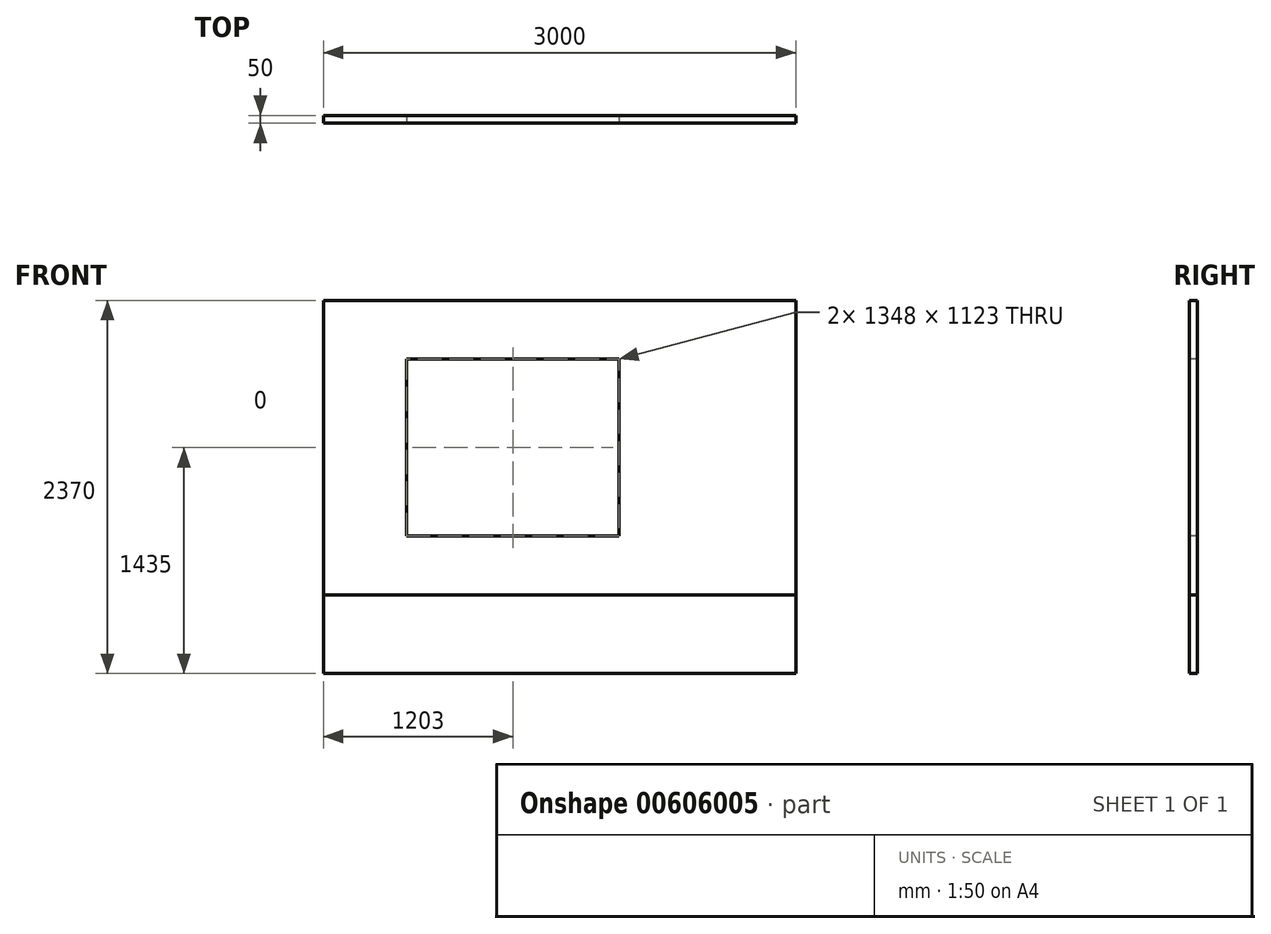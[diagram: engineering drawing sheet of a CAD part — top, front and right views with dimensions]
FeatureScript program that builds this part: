
annotation { "Feature Type Name" : "Feature", "Feature Type Description" : "" }
export const myFeature = defineFeature(function(context is Context, id is Id, definition is map)
    precondition{}
    {
        {
            var Q0;
            Q0=qCreatedBy(makeId("Front.planeOp"),FACE);
            var sketch = newSketch(context, id + "F0", { "sketchPlane" : qUnion([Q0])});
            skLineSegment(sketch, "E0.bottom", {"start": v(1500, -935) * mm, "end": v(-1500, -935) * mm});
            skLineSegment(sketch, "E0.top", {"start": v(1500, 935) * mm, "end": v(-1500, 935) * mm});
            skLineSegment(sketch, "E0.left", {"start": v(1500, -935) * mm, "end": v(1500, 935) * mm});
            skLineSegment(sketch, "E0.right", {"start": v(-1500, -935) * mm, "end": v(-1500, 935) * mm});
            skPoint(sketch, "E0.middle", {"position": v(0, 0) * mm});
            skSolve(sketch);
        }
        {
            var Q0;
            Q0=makeQuery(id+"F0.imprint","IMPRINT",FACE,{"disambiguationData":[TD([[makeQuery(id+"F0.imprint","IMPRINT",EDGE,{"derivedFrom":sQuery(id+"F0.wireOp",EDGE,"E0.bottom")}),-1.0]])]});
            extrude(context, id + "F1", {"entities" : qUnion([Q0]), "depth" : 50 * mm, "offsetDistance" : 25 * mm});
        }
        {
            var Q0;
            Q0=makeQuery(id+"F1.opExtrude","CAP_FACE",FACE,{"disambiguationData":[OSD([sQuery(id+"F0.wireOp",EDGE,"E0.bottom"),sQuery(id+"F0.wireOp",EDGE,"E0.top"),sQuery(id+"F0.wireOp",EDGE,"E0.left"),sQuery(id+"F0.wireOp",EDGE,"E0.right")])],"isStart":false});
            var sketch = newSketch(context, id + "F2", { "sketchPlane" : qUnion([Q0])});
            skLineSegment(sketch, "E1.bottom", {"start": v(-971, 561.5) * mm, "end": v(377, 561.5) * mm});
            skLineSegment(sketch, "E1.top", {"start": v(-971, -561.5) * mm, "end": v(377, -561.5) * mm});
            skLineSegment(sketch, "E1.left", {"start": v(-971, 561.5) * mm, "end": v(-971, -561.5) * mm});
            skLineSegment(sketch, "E1.right", {"start": v(377, 561.5) * mm, "end": v(377, -561.5) * mm});
            skSolve(sketch);
        }
        {
            var Q0;
            Q0 = qSketchRegion(id + "F2", true);
            extrude(context, id + "F3", {"entities" : qUnion([Q0]), "operationType" : NewBodyOperationType.REMOVE, "endBound" : BoundingType.UP_TO_NEXT, "oppositeDirection" : true, "depth" : 25 * mm, "offsetDistance" : 25 * mm});
        }
        {
            var Q0;
            Q0=makeQuery(id+"F1.opExtrude","SWEPT_FACE",FACE,{"disambiguationData":[OSD([sQuery(id+"F0.wireOp",EDGE,"E0.bottom")])]});
            extrude(context, id + "F4", {"entities" : qUnion([Q0]), "depth" : 500 * mm, "offsetDistance" : 25 * mm});
        }
    });
